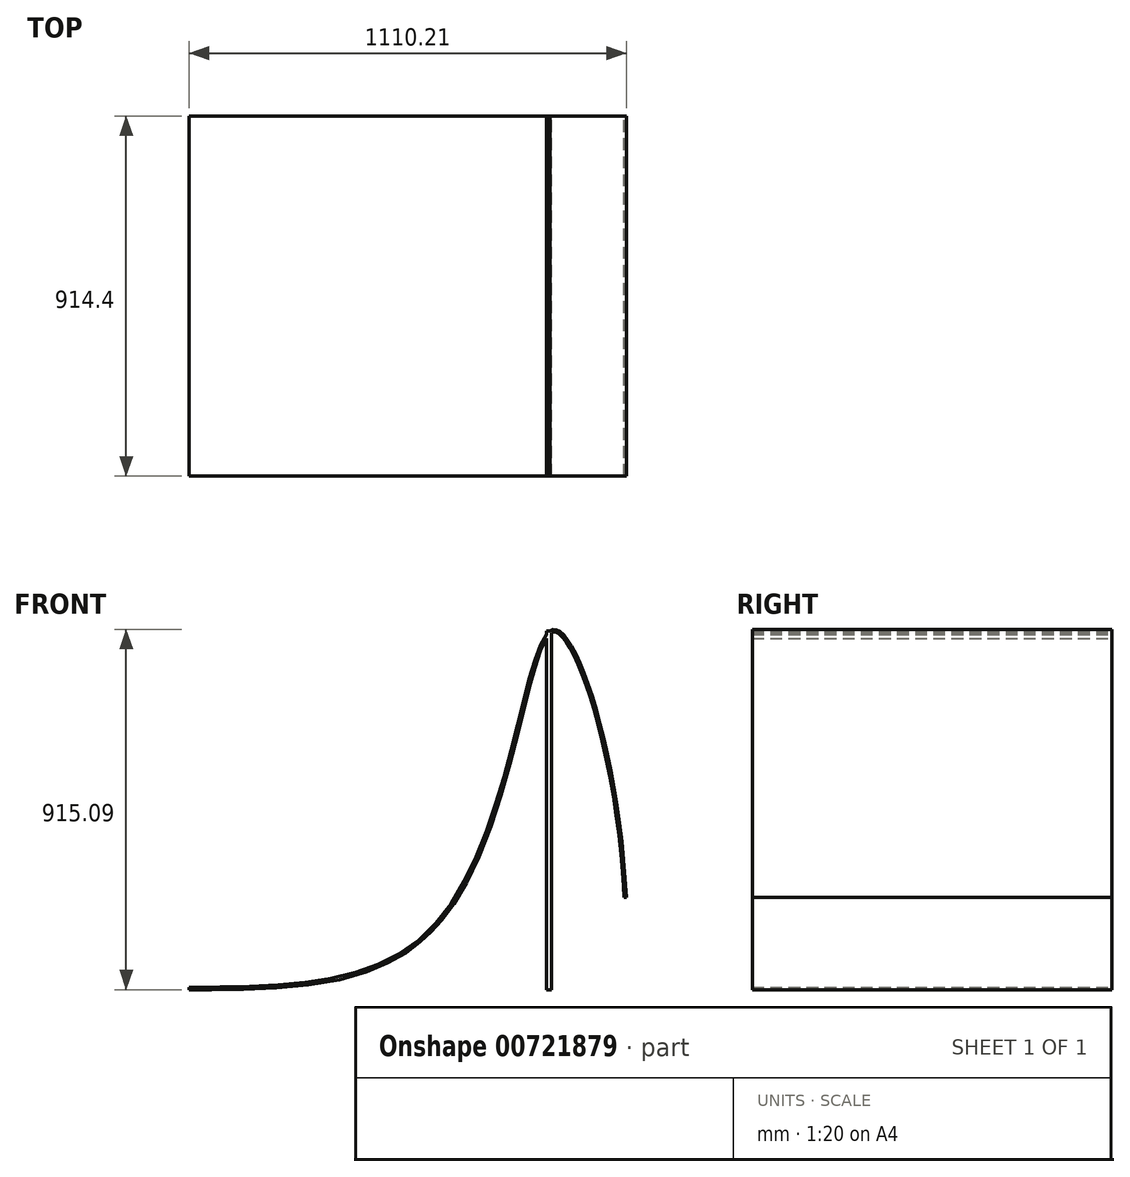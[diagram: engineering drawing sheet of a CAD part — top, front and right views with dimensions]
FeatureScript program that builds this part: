
annotation { "Feature Type Name" : "Feature", "Feature Type Description" : "" }
export const myFeature = defineFeature(function(context is Context, id is Id, definition is map)
    precondition{}
    {
        {
            var Q0;
            Q0=qCreatedBy(makeId("Front.planeOp"),FACE);
            var sketch = newSketch(context, id + "F0", { "sketchPlane" : qUnion([Q0])});
            skFitSpline(sketch, "E0", {"points": [v(-919.84, 0) * mm, v(-310.24, 144.3) * mm, v(-63.5, 755.65) * mm, v(12.7, 908.05) * mm, v(190.37, 228.54) * mm], "startDerivative": vector(2739.1, 0) * mm, "endDerivative": vector(158.87, -3425.9) * mm});
            skFitSpline(sketch, "E1.0", {"points": [v(-919.84, -6.35) * mm, v(-891.3, -6.35) * mm, v(-835.07, -6.23) * mm, v(-753.7, -4.55) * mm, v(-675.65, -0.27) * mm, v(-601.3, 7.75) * mm, v(-531.03, 20.65) * mm, v(-476.17, 36.43) * mm, v(-434.72, 52.66) * mm, v(-404.9, 66.78) * mm, v(-376.4, 82.99) * mm, v(-353.82, 98.35) * mm, v(-336.48, 111.83) * mm, v(-323.84, 122.55) * mm, v(-311.58, 133.89) * mm, v(-299.7, 145.88) * mm, v(-288.23, 158.49) * mm, v(-273.44, 176.09) * mm, v(-255.9, 199.49) * mm, v(-236.25, 229.55) * mm, v(-211.83, 271.97) * mm, v(-184.42, 328.75) * mm, v(-155.86, 401) * mm, v(-131.03, 475.45) * mm, v(-109.3, 550.18) * mm, v(-90.1, 623.26) * mm, v(-75.7, 681.17) * mm, v(-64.84, 724.74) * mm, v(-56.95, 755.8) * mm, v(-49.26, 784.97) * mm, v(-41.68, 811.87) * mm, v(-34.12, 836.1) * mm, v(-26.52, 857.26) * mm, v(-20.1, 871.99) * mm, v(-14.94, 881.78) * mm, v(-11.07, 888.07) * mm, v(-7.23, 893.25) * mm, v(-3.47, 897.25) * mm, v(0.1, 900.05) * mm, v(2.86, 901.45) * mm, v(4.95, 902.08) * mm, v(6.48, 902.35) * mm, v(8.02, 902.4) * mm, v(9.63, 902.26) * mm, v(11.33, 901.88) * mm, v(13.17, 901.23) * mm, v(15.15, 900.3) * mm, v(17.98, 898.63) * mm, v(21.8, 895.73) * mm, v(26.73, 890.96) * mm, v(31.9, 884.9) * mm, v(37.26, 877.63) * mm, v(42.77, 869.18) * mm, v(50.26, 856.39) * mm, v(59.84, 837.67) * mm, v(71.5, 811.15) * mm, v(83.2, 780.89) * mm, v(94.81, 747.16) * mm, v(110.03, 697.97) * mm, v(128.24, 629.26) * mm, v(147.92, 537.48) * mm, v(164.52, 438.6) * mm, v(177.17, 334.8) * mm, v(182.38, 263.82) * mm, v(184.03, 228.25) * mm]});
            skLineSegment(sketch, "E2", {"start": v(-919.84, -6.35) * mm, "end": v(-919.84, 0) * mm});
            skLineSegment(sketch, "E3", {"start": v(184.03, 228.25) * mm, "end": v(190.37, 228.54) * mm});
            skLineSegment(sketch, "E4", {"start": v(12.7, 908.05) * mm, "end": v(12.7, -6.35) * mm, "construction": true});
            skLineSegment(sketch, "E5.bottom", {"start": v(-12.7, -6.35) * mm, "end": v(0, -6.35) * mm});
            skLineSegment(sketch, "E5.top", {"start": v(-12.7, 904.88) * mm, "end": v(0, 904.88) * mm});
            skLineSegment(sketch, "E5.left", {"start": v(-12.7, -6.35) * mm, "end": v(-12.7, 904.88) * mm});
            skLineSegment(sketch, "E5.right", {"start": v(0, -6.35) * mm, "end": v(0, 904.88) * mm});
            skLineSegment(sketch, "E6", {"start": v(-456.11, -6.35) * mm, "end": v(12.7, -6.35) * mm, "construction": true});
            skSolve(sketch);
        }
        {
            var Q0;
            Q0=qSketchRegion(id+"F0",true);
            extrude(context, id + "F1", {"entities" : qUnion([Q0]), "depth" : 914.4 * mm, "offsetDistance" : 25.4 * mm});
        }
    });
